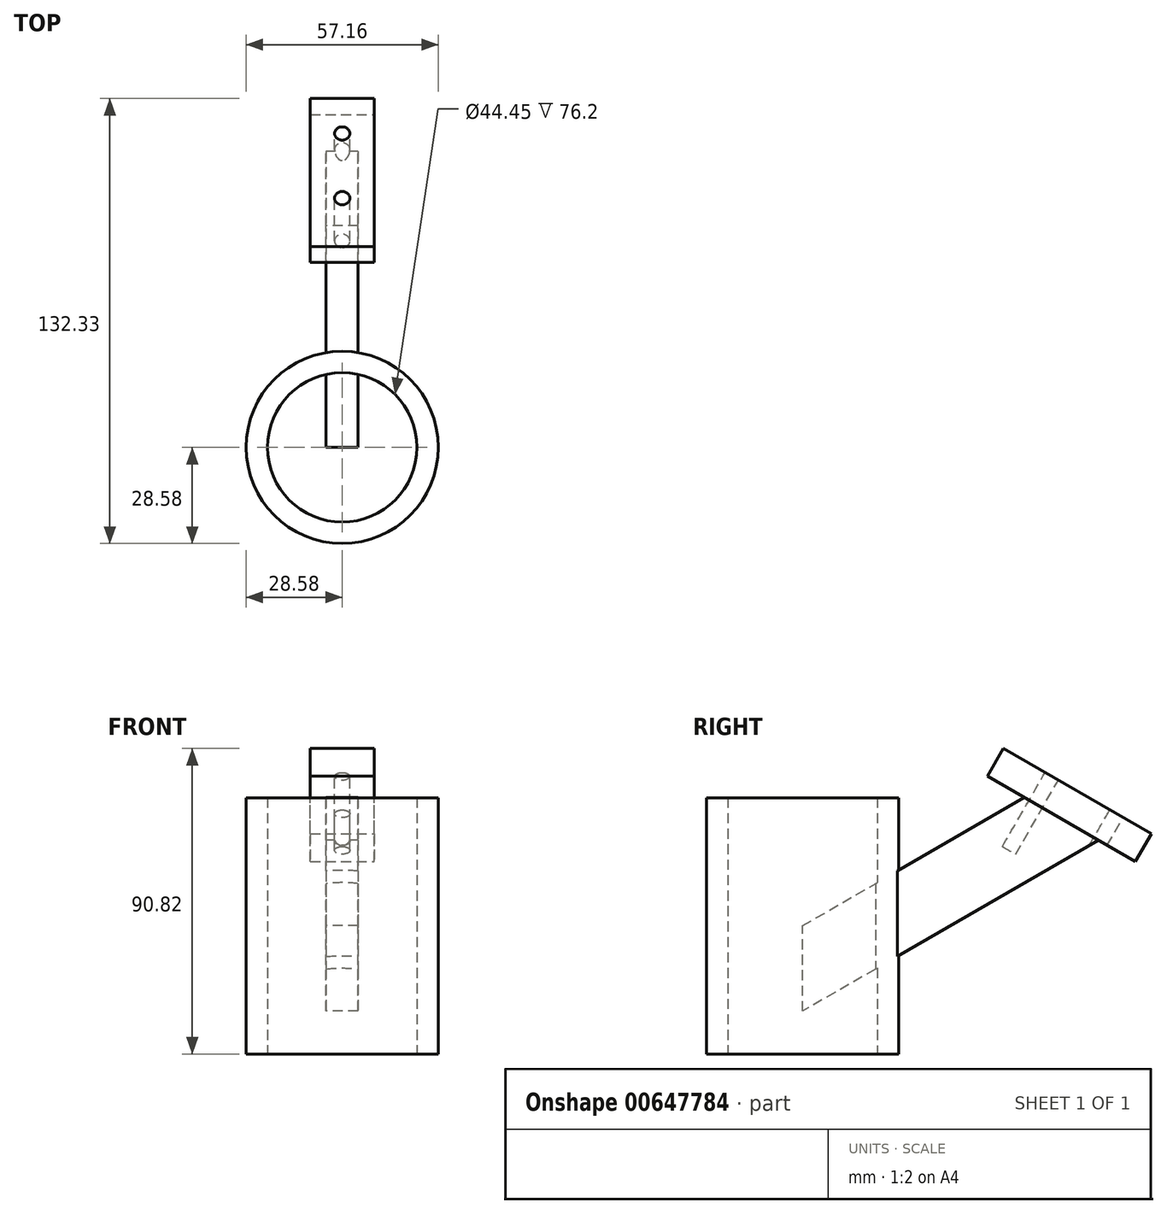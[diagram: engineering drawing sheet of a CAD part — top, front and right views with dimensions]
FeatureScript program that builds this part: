
annotation { "Feature Type Name" : "Feature", "Feature Type Description" : "" }
export const myFeature = defineFeature(function(context is Context, id is Id, definition is map)
    precondition{}
    {
        {
            var Q0;
            Q0=qCreatedBy(makeId("Top.planeOp"),FACE);
            var sketch = newSketch(context, id + "F0", { "sketchPlane" : qUnion([Q0])});
            skCircle(sketch, "E0", {"center": v(0, 0) * mm, "radius": 28.58 * mm});
            skCircle(sketch, "E1", {"center": v(0, 0) * mm, "radius": 22.23 * mm});
            skSolve(sketch);
        }
        {
            var Q0;
            Q0 = qSketchRegion(id + "F0", true);
            extrude(context, id + "F1", {"entities" : qUnion([Q0]), "depth" : 76.2 * mm, "offsetDistance" : 25.4 * mm});
        }
        {
            var Q0;
            Q0=qCreatedBy(makeId("Right.planeOp"),FACE);
            var sketch = newSketch(context, id + "F2", { "sketchPlane" : qUnion([Q0])});
            skLineSegment(sketch, "E2", {"start": v(0, 12.72) * mm, "end": v(0, 38.12) * mm});
            skLineSegment(sketch, "E3", {"start": v(0, 38.12) * mm, "end": v(66, 76.22) * mm});
            skLineSegment(sketch, "E4", {"start": v(66, 76.22) * mm, "end": v(87.99, 63.52) * mm});
            skLineSegment(sketch, "E5", {"start": v(87.99, 63.52) * mm, "end": v(0, 12.72) * mm});
            skSolve(sketch);
        }
        {
            var Q0;
            Q0=makeQuery(id+"F2.imprint","IMPRINT",FACE,{"disambiguationData":[TD([[makeQuery(id+"F2.imprint","IMPRINT",EDGE,{"derivedFrom":sQuery(id+"F2.wireOp",EDGE,"E2")}),-1.0]])]});
            extrude(context, id + "F3", {"entities" : qUnion([Q0]), "operationType" : NewBodyOperationType.ADD, "endBound" : BoundingType.SYMMETRIC, "depth" : 9.52 * mm, "offsetDistance" : 25.4 * mm});
        }
        {
            var Q0;
            Q0=makeQuery(id+"F3.opExtrude","SWEPT_FACE",FACE,{"disambiguationData":[OSD([sQuery(id+"F2.wireOp",EDGE,"E4")])]});
            var sketch = newSketch(context, id + "F4", { "sketchPlane" : qUnion([Q0])});
            skLineSegment(sketch, "E6", {"start": v(0, 19.04) * mm, "end": v(0, 44.44) * mm, "construction": true});
            skLineSegment(sketch, "E7", {"start": v(0, 44.44) * mm, "end": v(4.76, 31.74) * mm, "construction": true});
            skLineSegment(sketch, "E8", {"start": v(4.76, 31.74) * mm, "end": v(-4.76, 31.74) * mm, "construction": true});
            skLineSegment(sketch, "E9.bottom", {"start": v(-9.52, 57.14) * mm, "end": v(9.53, 57.14) * mm});
            skLineSegment(sketch, "E9.top", {"start": v(-9.52, 6.34) * mm, "end": v(9.53, 6.34) * mm});
            skLineSegment(sketch, "E9.left", {"start": v(-9.52, 57.14) * mm, "end": v(-9.52, 6.34) * mm});
            skLineSegment(sketch, "E9.right", {"start": v(9.53, 57.14) * mm, "end": v(9.53, 6.34) * mm});
            skPoint(sketch, "E9.middle", {"position": v(0, 31.74) * mm});
            skSolve(sketch);
        }
        {
            var Q0;
            Q0 = qSketchRegion(id + "F4", true);
            extrude(context, id + "F5", {"entities" : qUnion([Q0]), "operationType" : NewBodyOperationType.ADD, "depth" : 9.52 * mm, "offsetDistance" : 25.4 * mm});
        }
        {
            var Q0;
            Q0=makeQuery(id+"F5.opExtrude","CAP_FACE",FACE,{"disambiguationData":[OSD([sQuery(id+"F4.wireOp",EDGE,"E9.bottom"),sQuery(id+"F4.wireOp",EDGE,"E9.top"),sQuery(id+"F4.wireOp",EDGE,"E9.left"),sQuery(id+"F4.wireOp",EDGE,"E9.right")])],"isStart":false});
            var sketch = newSketch(context, id + "F6", { "sketchPlane" : qUnion([Q0])});
            skLineSegment(sketch, "E10", {"start": v(0, 57.14) * mm, "end": v(0, 6.34) * mm, "construction": true});
            skLineSegment(sketch, "E11", {"start": v(0, 6.34) * mm, "end": v(9.53, 31.74) * mm, "construction": true});
            skLineSegment(sketch, "E12", {"start": v(9.53, 31.74) * mm, "end": v(-9.52, 31.74) * mm, "construction": true});
            skCircle(sketch, "E13", {"center": v(0, 22.91) * mm, "radius": 2.29 * mm});
            skCircle(sketch, "E14", {"center": v(0, 45.14) * mm, "radius": 2.29 * mm});
            skSolve(sketch);
        }
        {
            var Q0;
            Q0 = qSketchRegion(id + "F6", true);
            extrude(context, id + "F7", {"entities" : qUnion([Q0]), "operationType" : NewBodyOperationType.REMOVE, "oppositeDirection" : true, "depth" : 25.4 * mm, "offsetDistance" : 25.4 * mm});
        }
    });
